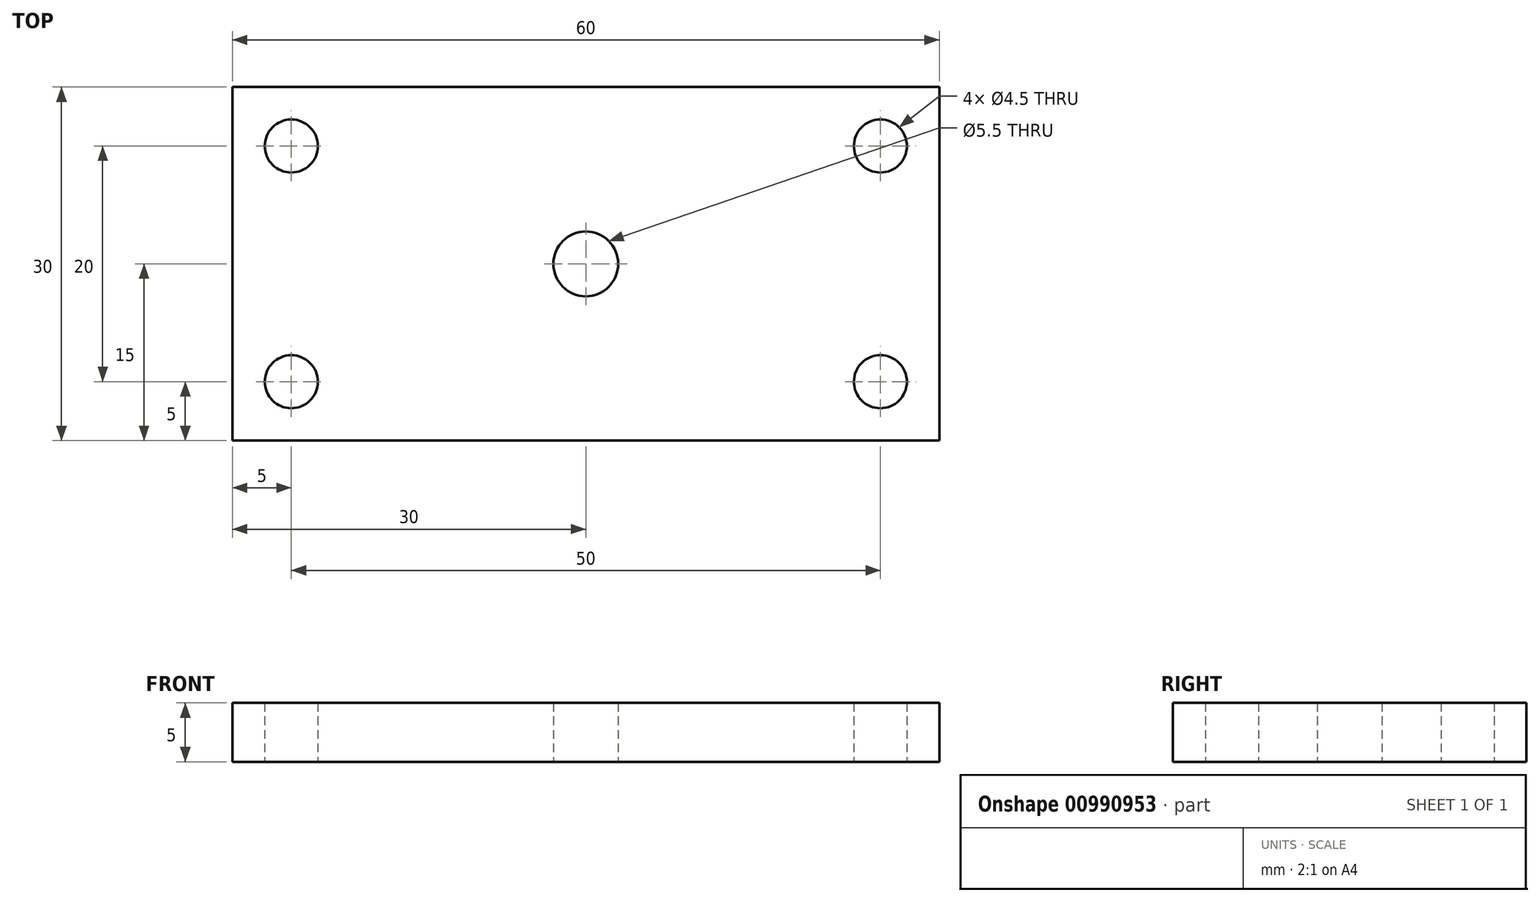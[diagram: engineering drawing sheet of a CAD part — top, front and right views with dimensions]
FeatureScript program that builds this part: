
annotation { "Feature Type Name" : "Feature", "Feature Type Description" : "" }
export const myFeature = defineFeature(function(context is Context, id is Id, definition is map)
    precondition{}
    {
        {
            var Q0;
            Q0=qCreatedBy(makeId("Top.planeOp"),FACE);
            var sketch = newSketch(context, id + "F0", { "sketchPlane" : qUnion([Q0])});
            skLineSegment(sketch, "E0.bottom", {"start": v(30, -15) * mm, "end": v(-30, -15) * mm});
            skLineSegment(sketch, "E0.top", {"start": v(30, 15) * mm, "end": v(-30, 15) * mm});
            skLineSegment(sketch, "E0.left", {"start": v(30, -15) * mm, "end": v(30, 15) * mm});
            skLineSegment(sketch, "E0.right", {"start": v(-30, -15) * mm, "end": v(-30, 15) * mm});
            skArc(sketch, "E1", {"start": v(2.44, -6.56) * mm, "mid": v(0.07, 7) * mm, "end": v(-2.56, -6.51) * mm});
            skCircle(sketch, "E2", {"center": v(0, 0) * mm, "radius": 12 * mm});
            skLineSegment(sketch, "E3", {"start": v(-30, 10) * mm, "end": v(30, 10) * mm, "construction": true});
            skLineSegment(sketch, "E4", {"start": v(-30, -10) * mm, "end": v(30, -10) * mm, "construction": true});
            skLineSegment(sketch, "E5", {"start": v(-25, -15) * mm, "end": v(-25, 15) * mm, "construction": true});
            skLineSegment(sketch, "E6", {"start": v(25, 15) * mm, "end": v(25, -15) * mm, "construction": true});
            skLineSegment(sketch, "E7", {"start": v(0, 15) * mm, "end": v(0, -15) * mm, "construction": true});
            skLineSegment(sketch, "E8", {"start": v(-2.56, -6.51) * mm, "end": v(-2.56, -9.5) * mm});
            skLineSegment(sketch, "E9", {"start": v(-2.56, -9.5) * mm, "end": v(2.44, -9.5) * mm});
            skLineSegment(sketch, "E10", {"start": v(2.44, -9.5) * mm, "end": v(2.44, -6.56) * mm});
            skPoint(sketch, "E11", {"position": v(0, -7) * mm});
            skCircle(sketch, "E12", {"center": v(-25, 10) * mm, "radius": 2.19 * mm});
            skCircle(sketch, "E13", {"center": v(25, 10) * mm, "radius": 1.56 * mm});
            skCircle(sketch, "E14", {"center": v(-25, -10) * mm, "radius": 2.33 * mm});
            skCircle(sketch, "E15", {"center": v(25, -10) * mm, "radius": 2.3 * mm});
            skSolve(sketch);
        }
        {
            var Q0;
            Q0=makeQuery(id+"F0.imprint","IMPRINT",FACE,{"disambiguationData":[TD([[makeQuery(id+"F0.imprint","IMPRINT",EDGE,{"derivedFrom":sQuery(id+"F0.wireOp",EDGE,"E13")}),1.0]])]});
            var Q1;
            Q1=makeQuery(id+"F0.imprint","IMPRINT",FACE,{"disambiguationData":[TD([[makeQuery(id+"F0.imprint","IMPRINT",EDGE,{"derivedFrom":sQuery(id+"F0.wireOp",EDGE,"E0.bottom")}),-1.0]])]});
            var Q2;
            Q2=makeQuery(id+"F0.imprint","IMPRINT",FACE,{"disambiguationData":[TD([[makeQuery(id+"F0.imprint","IMPRINT",EDGE,{"derivedFrom":sQuery(id+"F0.wireOp",EDGE,"E1")}),-1.0]])]});
            var Q3;
            Q3=makeQuery(id+"F0.imprint","IMPRINT",FACE,{"disambiguationData":[TD([[makeQuery(id+"F0.imprint","IMPRINT",EDGE,{"derivedFrom":sQuery(id+"F0.wireOp",EDGE,"E12")}),1.0]])]});
            var Q4;
            Q4=makeQuery(id+"F0.imprint","IMPRINT",FACE,{"disambiguationData":[TD([[makeQuery(id+"F0.imprint","IMPRINT",EDGE,{"derivedFrom":sQuery(id+"F0.wireOp",EDGE,"E15")}),1.0]])]});
            var Q5;
            Q5=makeQuery(id+"F0.imprint","IMPRINT",FACE,{"disambiguationData":[TD([[makeQuery(id+"F0.imprint","IMPRINT",EDGE,{"derivedFrom":sQuery(id+"F0.wireOp",EDGE,"E14")}),1.0]])]});
            var Q6;
            Q6=makeQuery(id+"F0.imprint","IMPRINT",FACE,{"disambiguationData":[TD([[makeQuery(id+"F0.imprint","IMPRINT",EDGE,{"derivedFrom":sQuery(id+"F0.wireOp",EDGE,"E1")}),1.0]])]});
            extrude(context, id + "F1", {"entities" : qUnion([Q0, Q1, Q2, Q3, Q4, Q5, Q6]), "depth" : 5 * mm, "offsetDistance" : 25 * mm});
        }
        {
            var Q0;
            Q0=sQuery(id+"F0.wireOp",VERTEX,"E13.center");
            var Q1;
            Q1=sQuery(id+"F0.wireOp",VERTEX,"E12.center");
            var Q2;
            Q2=sQuery(id+"F0.wireOp",VERTEX,"E14.center");
            var Q3;
            Q3=sQuery(id+"F0.wireOp",VERTEX,"E15.center");
            var Q4;
            Q4=makeQuery(id+"F1.opExtrude","SWEPT_BODY",BODY,{"disambiguationData":[OSD([sQuery(id+"F0.wireOp",EDGE,"E0.bottom"),sQuery(id+"F0.wireOp",EDGE,"E0.top"),sQuery(id+"F0.wireOp",EDGE,"E0.left"),sQuery(id+"F0.wireOp",EDGE,"E0.right")])]});
            hole(context, id + "F2", {"style" : HoleStyle.SIMPLE, "endStyle" : HoleEndStyle.THROUGH, "oppositeDirection" : true, "standardTappedOrClearance" : lookupTablePath({ "fit" : "Normal", "standard" : "ISO", "size" : "M4", "type" : "Clearance" }), "standardBlindInLast" : lookupTablePath({ "fit" : "Normal", "standard" : "ISO", "engagement" : "75%", "pitch" : "0.7 mm", "size" : "M4", "type" : "Clearance & tapped" }), "holeDiameter" : 4.5 * mm, "majorDiameter" : 5 * mm, "isTappedThrough" : true, "tappedDepth" : 12 * mm, "tapClearance" : 3, "locations" : qUnion([Q0, Q1, Q2, Q3]), "scope" : qUnion([Q4])});
        }
        {
            var Q0;
            Q0=sQuery(id+"F0.wireOp",VERTEX,"E1.center");
            var Q1;
            Q1=makeQuery(id+"F1.opExtrude","SWEPT_BODY",BODY,{"disambiguationData":[OSD([sQuery(id+"F0.wireOp",EDGE,"E0.bottom"),sQuery(id+"F0.wireOp",EDGE,"E0.top"),sQuery(id+"F0.wireOp",EDGE,"E0.left"),sQuery(id+"F0.wireOp",EDGE,"E0.right")])]});
            hole(context, id + "F3", {"style" : HoleStyle.SIMPLE, "endStyle" : HoleEndStyle.THROUGH, "oppositeDirection" : true, "standardTappedOrClearance" : lookupTablePath({ "fit" : "Normal", "standard" : "ISO", "size" : "M5", "type" : "Clearance" }), "standardBlindInLast" : lookupTablePath({ "fit" : "Normal", "standard" : "ISO", "engagement" : "75%", "pitch" : "0.8 mm", "size" : "M5", "type" : "Clearance & tapped" }), "holeDiameter" : 5.5 * mm, "majorDiameter" : 5 * mm, "isTappedThrough" : true, "tappedDepth" : 12 * mm, "tapClearance" : 3, "locations" : qUnion([Q0]), "scope" : qUnion([Q1])});
        }
    });
